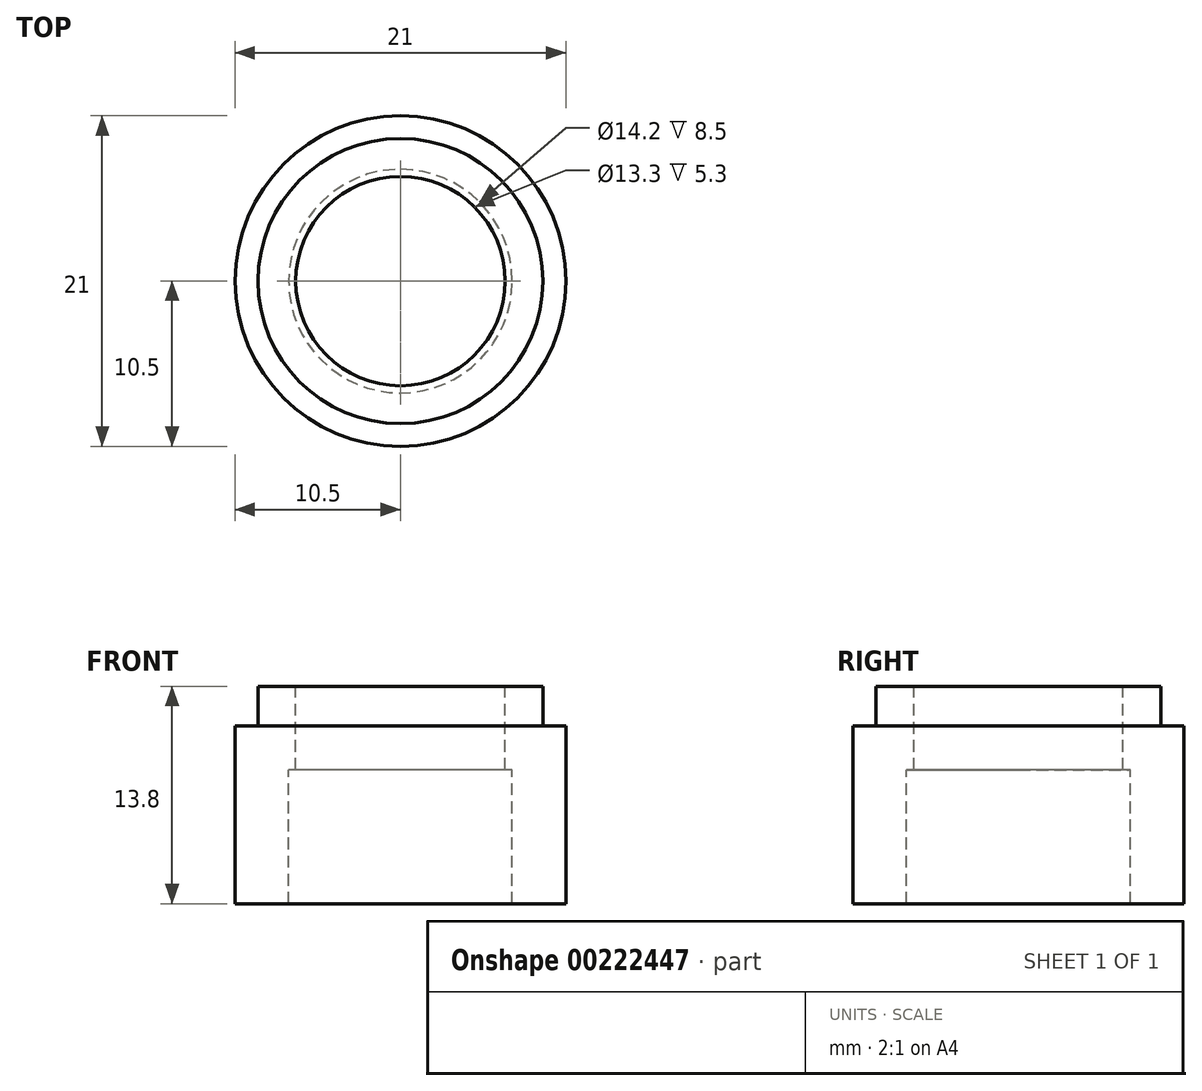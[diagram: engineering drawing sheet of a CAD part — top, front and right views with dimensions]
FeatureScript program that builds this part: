
annotation { "Feature Type Name" : "Feature", "Feature Type Description" : "" }
export const myFeature = defineFeature(function(context is Context, id is Id, definition is map)
    precondition{}
    {
        {
            var Q0;
            Q0=qCreatedBy(makeId("Front.planeOp"),FACE);
            var sketch = newSketch(context, id + "F0", { "sketchPlane" : qUnion([Q0])});
            skLineSegment(sketch, "E0", {"start": v(0, 20.14) * mm, "end": v(0, -20.84) * mm, "construction": true});
            skLineSegment(sketch, "E1", {"start": v(-7.1, 0) * mm, "end": v(-10.5, 0) * mm});
            skLineSegment(sketch, "E2", {"start": v(-10.5, 11.3) * mm, "end": v(-9.05, 11.3) * mm});
            skLineSegment(sketch, "E3", {"start": v(-9.05, 11.3) * mm, "end": v(-9.05, 13.8) * mm});
            skLineSegment(sketch, "E4", {"start": v(-9.05, 13.8) * mm, "end": v(-6.65, 13.8) * mm});
            skLineSegment(sketch, "E5", {"start": v(-6.65, 13.8) * mm, "end": v(-6.65, 8.5) * mm});
            skLineSegment(sketch, "E6", {"start": v(-6.65, 8.5) * mm, "end": v(-7.1, 8.5) * mm});
            skLineSegment(sketch, "E7", {"start": v(-7.1, 8.5) * mm, "end": v(-7.1, 0) * mm});
            skLineSegment(sketch, "E8", {"start": v(-10.5, 11.3) * mm, "end": v(-10.5, 0) * mm});
            skSolve(sketch);
        }
        {
            var Q0;
            Q0 = qSketchRegion(id + "F0", true);
            var Q1;
            Q1=sQuery(id+"F0.wireOp",EDGE,"E0");
            revolve(context, id + "F1", {"entities" : qUnion([Q0]), "axis" : qUnion([Q1]), "revolveType" : RevolveType.FULL});
        }
    });
